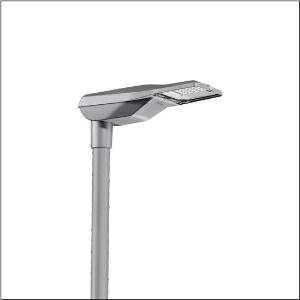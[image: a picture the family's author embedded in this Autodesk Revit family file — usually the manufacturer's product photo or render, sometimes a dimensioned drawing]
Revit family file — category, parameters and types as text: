
# Revit family: streetlight_sl_21_iq_micro___st1_0a_5xe1d61g08cb_d415
name_source: partatom
category: Lighting Fixtures
units: mm (PartAtom-declared; Revit-internal decimal feet)

## family parameters
Cut with Voids When Loaded = No
Host = Face
Light Source = No
Part Type = Normal
Room Calculation Point = No
Round Connector Dimension = Use Diameter
Shared = No

## types (1)
- --- (1 x LED, 2570 lm, 19.4 W, 2700K)
    Apparent Load = 19 VA
    CIE Flux Codes = 37 72 97 100 100
    Color Rendering = 70
    Color Temperature = 2700K
    Default Elevation = 1800 mm
    Description = Streetlight SL 21 iQ micro, mast luminaire, primary light control with lens, of PMMA, primary optical cover: cover, of toughened safety glass, transparent, light distribution: ST1.0a, light emission: direct distribution, primary light characteristic: asymmetric, installation type: post-top, side-entry, LED, High Power LED, rated luminous flux: 2.570lm, luminous efficacy: 133lm/W, light colour: 727, colour temperature: 2700K, control: Street-Remote, Auto-Match, Temp-Guard, Lumen-Switch, Night-Set, Smart-Wire, Light-Fading, Desk-Remote (wireless, voltage-free reading and setting of iQ features in the workshop via application-optimized NFC function/RFID function), optimised constant luminous flux control (CLO 2.0), presetting dimming linear, mains connection: 220..240V, AC, 50/60Hz, start of lifetime: 19W, end of service life: 20W, reduction: 10W, luminaire housing, of diecast aluminium, powder-coated, Siteco® metallic grey (DB 702S), corrosivity category C5 mid according to DIN EN ISO 12944, please order mast flange separately, inclination adjustable: 0°, 5°, 10°, 15°, sealing non-destructively replaceable, multi-level sealing system, length: 528mm, width: 235mm, height: 110mm, mast flange for spigot size: 42mm (side-entry): 5XC10008XM4, 60/48mm (side-entry/post-top): 5XC10108XM2, 76/60mm (side-entry/post-top): 5XC10108XM1, protection rating (complete): IP66, insulation class (complete): insulation class II (safety insulation), certification: CE, ENEC, ENEC+, VDE, impact resistance: IK09, permissible operating ambient temperature for outdoor applications: -40..+50°C, standard-compliant lighting for roads and squares, packaging unit: 1 piece

Light Distribution: ST1.0a
    Height = 110 mm
    Lamp = 1 x LED
    Lamp Light Flux = 2570 lm
    Lamp Power = 19.4 W
    Lamp count = 1
    Length = 528 mm
    Luminous efficacy = 132 lm/W
    Manufacturer = Siteco
    ModVariant = No
    Model = 5XE1D61G08CB
    Number of Poles = 1
    OnlyDefault = Yes
    Power Factor = 1
    Product Name = Streetlight SL 21 iQ micro | ST1.0a
    Product group = mast luminaire | pylon top
    ProductGroupID = 6100
    Protection Class = Protection class II
    Protection Degree = IP 66
    RLX_Detail_Level = 1
    RLX_Emergency_Light_Flux = 0 lm
    RLX_Emergency_Type = 0
    RLX_Emergency_Type_DB = No
    RlxData = <blob elided: 98325 chars, md5=058a7ee3>
    Socket = socket
    Standby Power = 0 W
    System Light Flux = 2570 lm
    System Power = 19 W
    Type Comments = factory setting: luminous flux: 100 % | dim-lin: 254 | 387 mA
    Type Image = l_1006881.jpg
    URL = http://relux.com
    VarID = @adj_070433
    Voltage = 0 V
    Weight = 0.00 kg
    Width = 235 mm

## geometry (parser evidence)
native form markers: Blend x4, Sweep x10
no freeform markers — native parametric forms only
